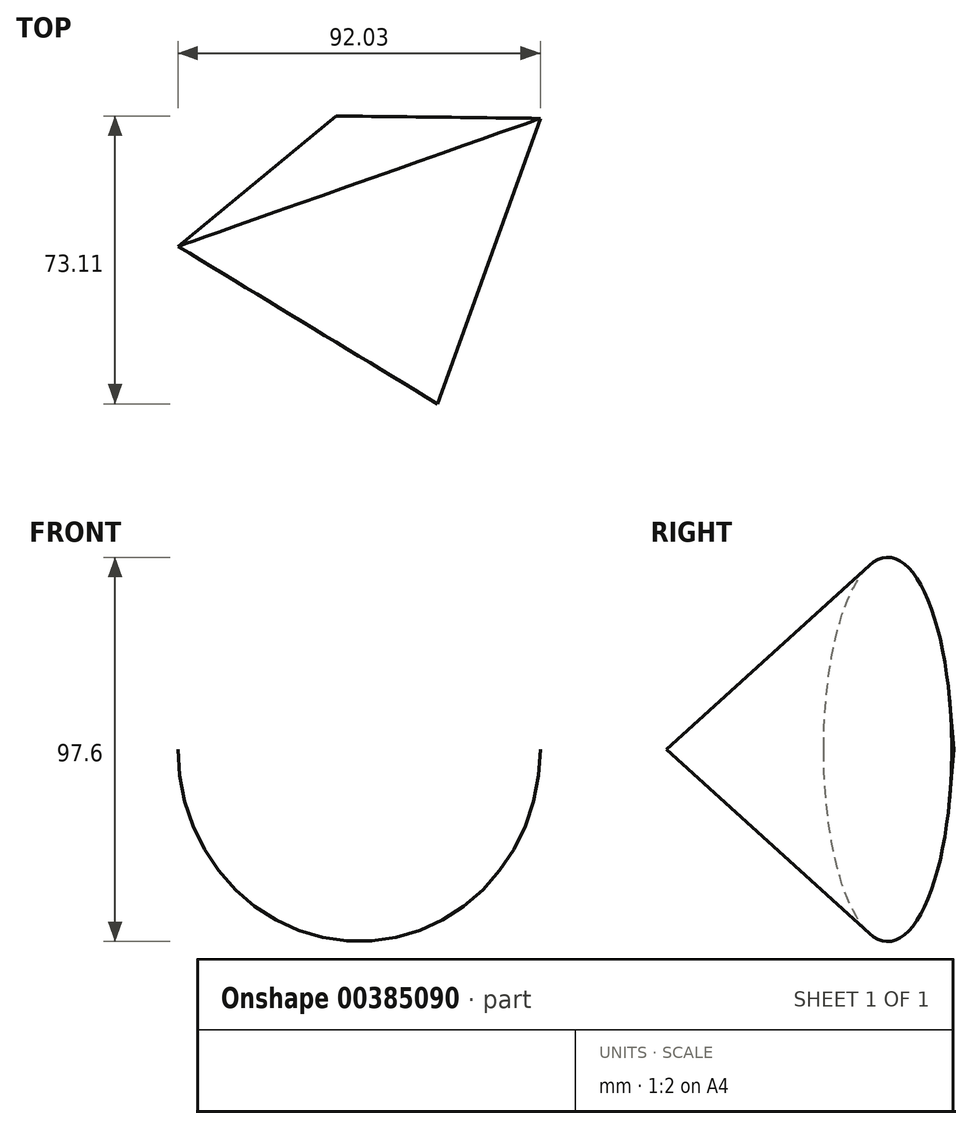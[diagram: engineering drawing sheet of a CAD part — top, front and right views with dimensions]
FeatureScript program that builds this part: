
annotation { "Feature Type Name" : "Feature", "Feature Type Description" : "" }
export const myFeature = defineFeature(function(context is Context, id is Id, definition is map)
    precondition{}
    {
        {
            var Q0;
            Q0=qCreatedBy(makeId("Top.planeOp"),FACE);
            var sketch = newSketch(context, id + "F0", { "sketchPlane" : qUnion([Q0])});
            skLineSegment(sketch, "E0", {"start": v(-5.43, 28.33) * mm, "end": v(20.4, -44.78) * mm});
            skLineSegment(sketch, "E1", {"start": v(20.4, -44.78) * mm, "end": v(46.54, 27.75) * mm});
            skLineSegment(sketch, "E2", {"start": v(46.54, 27.75) * mm, "end": v(-5.43, 28.33) * mm});
            skSolve(sketch);
        }
        {
            var Q0;
            Q0=makeQuery(id+"F0.imprint","IMPRINT",FACE,{"disambiguationData":[TD([[makeQuery(id+"F0.imprint","IMPRINT",EDGE,{"derivedFrom":sQuery(id+"F0.wireOp",EDGE,"E0")}),1.0]])]});
            var Q1;
            Q1=sQuery(id+"F0.wireOp",EDGE,"E0");
            revolve(context, id + "F1", {"entities" : qUnion([Q0]), "axis" : qUnion([Q1]), "revolveType" : RevolveType.FULL});
        }
    });
